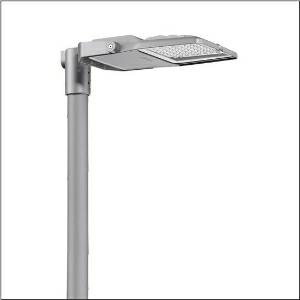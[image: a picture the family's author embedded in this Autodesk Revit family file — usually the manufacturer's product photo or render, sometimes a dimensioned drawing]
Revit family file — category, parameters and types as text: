
# Revit family: floodlight_fl_21_iq_mini___pl61_5xa7772d4c3a_23c5
name_source: partatom
category: Lighting Fixtures
units: mm (PartAtom-declared; Revit-internal decimal feet)

## family parameters
Cut with Voids When Loaded = No
Host = Face
Light Source = No
Part Type = Normal
Room Calculation Point = No
Round Connector Dimension = Use Diameter
Shared = No

## types (1)
- --- (1 x LED, 18260 lm, 143 W, 4000K)
    Apparent Load = 143 VA
    CIE Flux Codes = 33 65 98 100 100
    Color Rendering = 70
    Color Temperature = 4000K
    Default Elevation = 1800 mm
    Description = Floodlight FL 21 iQ mini, floodlight, primary light control with lens, of PMMA, primary optical cover: protective disc, of toughened safety glass, transparent, light distribution: PL61, light emission: direct distribution, installation type: surface-mounted, lamps: LED, High Power LED, rated values: 18.260lm | 143W | 127,7lm/W (begin service life); end service life: 18.260lm | 151,6W; at 50% lumin. flux: 9.130lm | 60,8W | 150,2lm/W, colour temperature: 4000K, colour rendering: CRI > 70, light colour: 740, light setting 1 begin service life: 100% | 18.260lm | 143W | 127,7lm/W | 4.000K, light setting 1 end service life: 151,6W, further light settings possible, control: pre-setting: linear dimming characteristic, Auto-Match, Temp-Guard, Night-Set, Smart-Wire, Desk-Remote (wireless, voltage-free reading and setting of iQ features in the workshop via application-optimized NFC function/RFID function), optimised constant luminous flux control (CLO 2.0), Light-Fading, Lumen-Switch, with terminal, 6-pole, mains connection: 220..240V, AC, 50/60Hz, luminaire housing, of diecast aluminium, powder-coated, SITECO metallic grey (DB 702S), corrosivity category C5 mid according to DIN EN ISO 12944suitable for swimming poolschlorine-resistant, sealing non-destructively replaceable, please order mast flange separately, mast bracket, of steel, galvanised, powder-coated, protection rating (complete): IP66, insulation class (complete): insulation class II (safety insulation), certification: CE, ENEC, VDE, protection symbol: D, impact resistance: IK08, permissible operating ambient temperature: -40..+40°C, permissible operating ambient temperature for outdoor applications: -40..+50°C, standard: DIN EN 12944, LABS conformity tested according to VDMA 24364:2018-05, packaging unit: 1 piece

Light Distribution: PL61
    Height = 70 mm
    Lamp = 1 x LED
    Lamp Light Flux = 18260 lm
    Lamp Power = 143 W
    Lamp count = 1
    Length = 485 mm
    Luminous efficacy = 128 lm/W
    Manufacturer = Siteco
    ModVariant = No
    Model = 5XA7772D4C3A
    Number of Poles = 1
    OnlyDefault = Yes
    Power Factor = 1
    Product Name = Floodlight FL 21 iQ mini | PL61
    Product group = floodlight | pylon annexe
    ProductGroupID = 6201
    Protection Class = Protection class II
    Protection Degree = IP 66
    RLX_Detail_Level = 1
    RLX_Emergency_Light_Flux = 0 lm
    RLX_Emergency_Type = 0
    RLX_Emergency_Type_DB = No
    RlxData = <blob elided: 101905 chars, md5=f10922fa>
    Socket = socket
    Standby Power = 0 W
    System Light Flux = 18260 lm
    System Power = 143 W
    Type Comments = factory setting: luminous flux: 100 % | dim-lin: 254 | 730 mA
    Type Image = l_1007125.jpg
    URL = http://relux.com
    VarID = @adj_171785
    Voltage = 0 V
    Weight = 0.00 kg
    Width = 337 mm

## geometry (parser evidence)
native form markers: Blend x4, Sweep x11
no freeform markers — native parametric forms only
